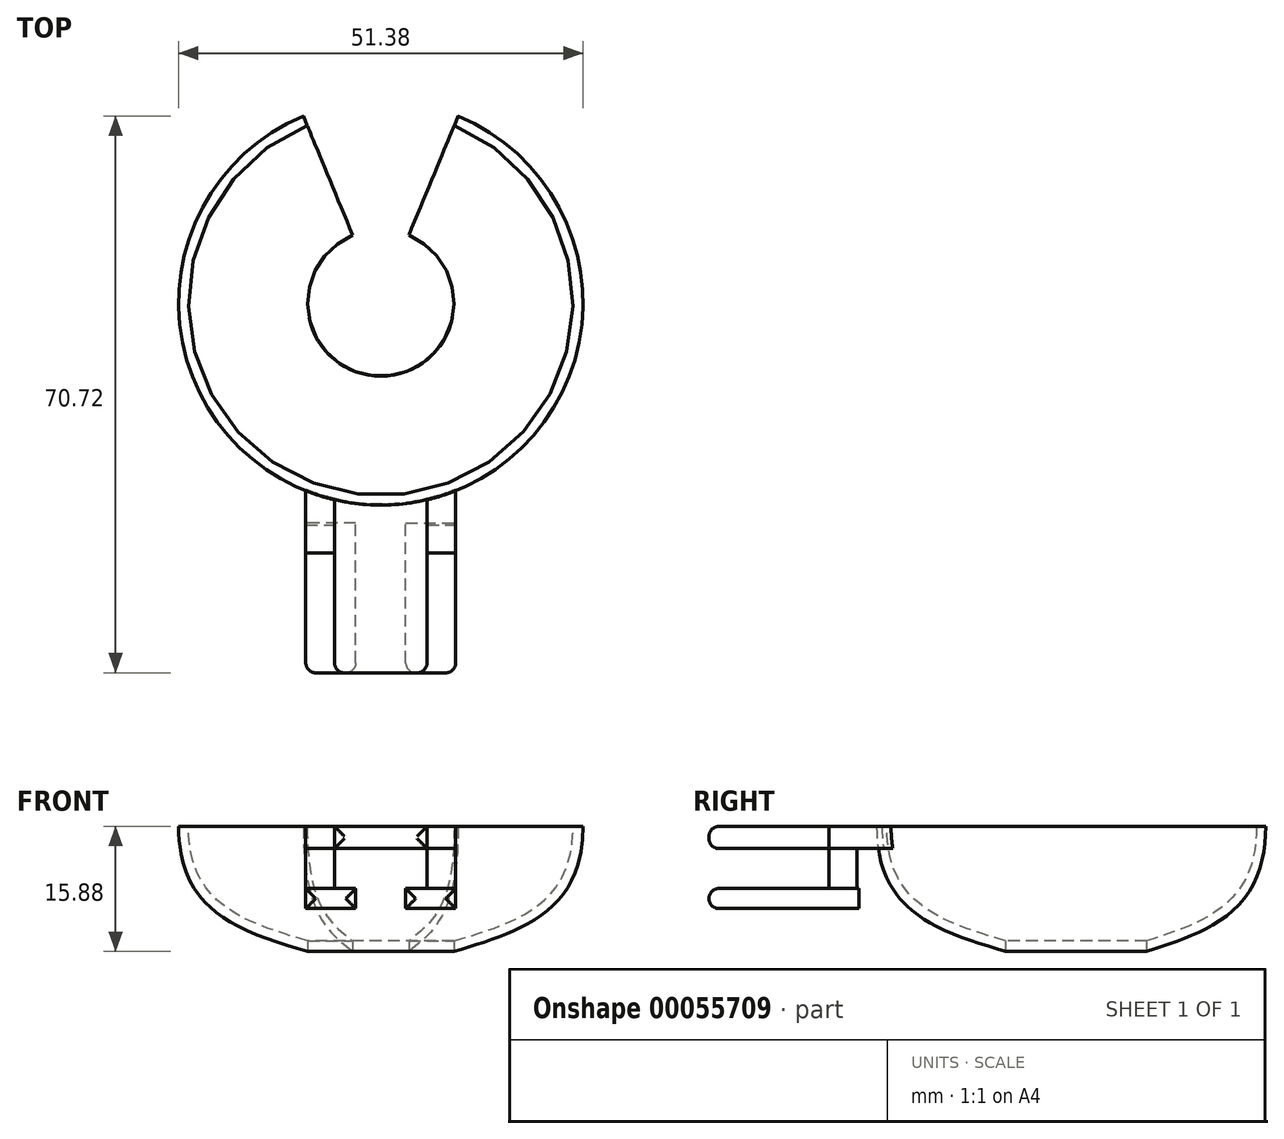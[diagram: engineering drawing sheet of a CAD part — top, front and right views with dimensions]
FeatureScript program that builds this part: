
annotation { "Feature Type Name" : "Feature", "Feature Type Description" : "" }
export const myFeature = defineFeature(function(context is Context, id is Id, definition is map)
    precondition{}
    {
        {
            var Q0;
            Q0=qCreatedBy(makeId("Top.planeOp"),FACE);
            var sketch = newSketch(context, id + "F0", { "sketchPlane" : qUnion([Q0])});
            skCircle(sketch, "E0", {"center": v(0, 0) * mm, "radius": 18.62 * mm});
            skSolve(sketch);
        }
        {
            var Q0;
            Q0=qCreatedBy(makeId("Top.planeOp"),FACE);
            cPlane(context, id + "F1", {"entities" : qUnion([Q0]), "cplaneType" : CPlaneType.OFFSET, "offset" : 31.75 * mm, "width" : 152.4 * mm, "height" : 152.4 * mm});
        }
        {
            var Q0;
            Q0=qCreatedBy(id+"F1.planeOp",FACE);
            var sketch = newSketch(context, id + "F2", { "sketchPlane" : qUnion([Q0])});
            skCircle(sketch, "E1", {"center": v(0, 0) * mm, "radius": 51.37 * mm});
            skSolve(sketch);
        }
        {
            var Q0;
            Q0=makeQuery(id+"F0.imprint","IMPRINT",FACE,{"disambiguationData":[TD([[makeQuery(id+"F0.imprint","IMPRINT",EDGE,{"derivedFrom":sQuery(id+"F0.wireOp",EDGE,"E0")}),1.0]])]});
            var Q1;
            Q1=makeQuery(id+"F2.imprint","IMPRINT",FACE,{"disambiguationData":[TD([[makeQuery(id+"F2.imprint","IMPRINT",EDGE,{"derivedFrom":sQuery(id+"F2.wireOp",EDGE,"E1")}),1.0]])]});
            loft(context, id + "F3", {"endCondition" : LoftEndDerivativeType.NORMAL_TO_PROFILE, "endMagnitude" : 2, "sheetProfilesArray" : [{ "sheetProfileEntities" : qUnion([Q0]) }, { "sheetProfileEntities" : qUnion([Q1]) }]});
        }
        {
            var Q0;
            Q0=makeQuery(id+"F3.opLoft","CAP_FACE",FACE,{"disambiguationData":[OSD([makeQuery(id+"F2.imprint","IMPRINT",FACE,{"disambiguationData":[TD([[makeQuery(id+"F2.imprint","IMPRINT",EDGE,{"derivedFrom":sQuery(id+"F2.wireOp",EDGE,"E1")}),1.0]])]})])],"isStart":true});
            shell(context, id + "F4", {"entities" : qUnion([Q0]), "thickness" : 2.54 * mm});
        }
        {
            var Q0;
            Q0=makeQuery(id+"F3.opLoft","CAP_FACE",FACE,{"disambiguationData":[OSD([makeQuery(id+"F0.imprint","IMPRINT",FACE,{"disambiguationData":[TD([[makeQuery(id+"F0.imprint","IMPRINT",EDGE,{"derivedFrom":sQuery(id+"F0.wireOp",EDGE,"E0")}),1.0]])]})])],"isStart":true});
            extrude(context, id + "F5", {"entities" : qUnion([Q0]), "operationType" : NewBodyOperationType.REMOVE, "oppositeDirection" : true, "depth" : 25.4 * mm});
        }
        {
            var Q0;
            Q0=qCreatedBy(makeId("Front.planeOp"),FACE);
            cPlane(context, id + "F6", {"entities" : qUnion([Q0]), "cplaneType" : CPlaneType.OFFSET, "offset" : 55.88 * mm, "width" : 152.4 * mm, "height" : 152.4 * mm});
        }
        {
            var Q0;
            Q0=qCreatedBy(id+"F6.planeOp",FACE);
            var sketch = newSketch(context, id + "F7", { "sketchPlane" : qUnion([Q0])});
            skLineSegment(sketch, "E2.rect.bottom", {"start": v(11.76, 26.12) * mm, "end": v(-11.76, 26.12) * mm});
            skLineSegment(sketch, "E2.rect.top", {"start": v(11.76, 31.75) * mm, "end": v(-11.76, 31.75) * mm});
            skLineSegment(sketch, "E2.rect.left", {"start": v(11.76, 26.12) * mm, "end": v(11.76, 31.75) * mm});
            skLineSegment(sketch, "E2.rect.right", {"start": v(-11.76, 26.12) * mm, "end": v(-11.76, 31.75) * mm});
            skPoint(sketch, "E2.rect.middle", {"position": v(0, 28.94) * mm});
            skLineSegment(sketch, "E3.bottom", {"start": v(6.35, 15.96) * mm, "end": v(19.05, 15.96) * mm});
            skLineSegment(sketch, "E3.top", {"start": v(6.35, 10.88) * mm, "end": v(19.05, 10.88) * mm});
            skLineSegment(sketch, "E3.left", {"start": v(6.35, 15.96) * mm, "end": v(6.35, 10.88) * mm});
            skLineSegment(sketch, "E3.right", {"start": v(19.05, 15.96) * mm, "end": v(19.05, 10.88) * mm});
            skLineSegment(sketch, "E4.bottom", {"start": v(-6.35, 15.96) * mm, "end": v(-19.05, 15.96) * mm});
            skLineSegment(sketch, "E4.top", {"start": v(-6.35, 10.88) * mm, "end": v(-19.05, 10.88) * mm});
            skLineSegment(sketch, "E4.left", {"start": v(-6.35, 15.96) * mm, "end": v(-6.35, 10.88) * mm});
            skLineSegment(sketch, "E4.right", {"start": v(-19.05, 15.96) * mm, "end": v(-19.05, 10.88) * mm});
            skLineSegment(sketch, "E5.bottom", {"start": v(11.76, 31.75) * mm, "end": v(19.05, 31.75) * mm});
            skLineSegment(sketch, "E5.top", {"start": v(11.76, 26.12) * mm, "end": v(19.05, 26.12) * mm});
            skLineSegment(sketch, "E5.left", {"start": v(11.76, 31.75) * mm, "end": v(11.76, 26.12) * mm});
            skLineSegment(sketch, "E5.right", {"start": v(19.05, 31.75) * mm, "end": v(19.05, 26.12) * mm});
            skLineSegment(sketch, "E6.bottom", {"start": v(-11.76, 31.75) * mm, "end": v(-19.05, 31.75) * mm});
            skLineSegment(sketch, "E6.top", {"start": v(-11.76, 26.12) * mm, "end": v(-19.05, 26.12) * mm});
            skLineSegment(sketch, "E6.left", {"start": v(-11.76, 31.75) * mm, "end": v(-11.76, 26.12) * mm});
            skLineSegment(sketch, "E6.right", {"start": v(-19.05, 31.75) * mm, "end": v(-19.05, 26.12) * mm});
            skSolve(sketch);
        }
        {
            var Q0;
            Q0=makeQuery(id+"F7.imprint","IMPRINT",FACE,{"disambiguationData":[TD([[makeQuery(id+"F7.imprint","IMPRINT",EDGE,{"derivedFrom":sQuery(id+"F7.wireOp",EDGE,"E4.bottom")}),1.0]])]});
            var Q1;
            Q1=makeQuery(id+"F7.imprint","IMPRINT",FACE,{"disambiguationData":[TD([[makeQuery(id+"F7.imprint","IMPRINT",EDGE,{"derivedFrom":sQuery(id+"F7.wireOp",EDGE,"E3.bottom")}),-1.0]])]});
            extrude(context, id + "F8", {"entities" : qUnion([Q0, Q1]), "depth" : 38.1 * mm});
        }
        {
            var Q0;
            Q0=qCreatedBy(makeId("Right.planeOp"),FACE);
            var sketch = newSketch(context, id + "F9", { "sketchPlane" : qUnion([Q0])});
            skLineSegment(sketch, "E7.bottom", {"start": v(0, 57.73) * mm, "end": v(69.76, 57.73) * mm});
            skLineSegment(sketch, "E7.top", {"start": v(0, -10.02) * mm, "end": v(69.76, -10.02) * mm});
            skLineSegment(sketch, "E7.left", {"start": v(0, 57.73) * mm, "end": v(0, -10.02) * mm});
            skLineSegment(sketch, "E7.right", {"start": v(69.76, 57.73) * mm, "end": v(69.76, -10.02) * mm});
            skSolve(sketch);
        }
        {
            var Q0;
            Q0 = qSketchRegion(id + "F9", true);
            var Q1;
            Q1=sQuery(id+"F9.wireOp",EDGE,"E7.left");
            revolve(context, id + "F10", {"operationType" : NewBodyOperationType.REMOVE, "entities" : qUnion([Q0]), "axis" : qUnion([Q1]), "revolveType" : RevolveType.SYMMETRIC, "oppositeDirection" : true, "angle" : 45 * degree});
        }
        {
            var Q0;
            Q0=makeQuery(id+"F7.imprint","IMPRINT",FACE,{"disambiguationData":[TD([[makeQuery(id+"F7.imprint","IMPRINT",EDGE,{"derivedFrom":sQuery(id+"F7.wireOp",EDGE,"E5.bottom")}),-1.0]])]});
            var Q1;
            Q1=makeQuery(id+"F7.imprint","IMPRINT",FACE,{"disambiguationData":[TD([[makeQuery(id+"F7.imprint","IMPRINT",EDGE,{"derivedFrom":sQuery(id+"F7.wireOp",EDGE,"E6.bottom")}),1.0]])]});
            var Q2;
            Q2=makeQuery(id+"F3.opLoft","SWEPT_BODY",BODY,{"disambiguationData":[OSD([makeQuery(id+"F0.imprint","IMPRINT",FACE,{"disambiguationData":[TD([[makeQuery(id+"F0.imprint","IMPRINT",EDGE,{"derivedFrom":sQuery(id+"F0.wireOp",EDGE,"E0")}),1.0]])]}),makeQuery(id+"F2.imprint","IMPRINT",FACE,{"disambiguationData":[TD([[makeQuery(id+"F2.imprint","IMPRINT",EDGE,{"derivedFrom":sQuery(id+"F2.wireOp",EDGE,"E1")}),1.0]])]})])]});
            extrude(context, id + "F11", {"entities" : qUnion([Q0, Q1]), "endBound" : BoundingType.UP_TO_NEXT, "oppositeDirection" : true, "endBoundEntityBody" : qUnion([Q2]), "depth" : 25.4 * mm, "hasSecondDirection" : true, "secondDirectionOppositeDirection" : false, "secondDirectionDepth" : 7.62 * mm});
        }
        {
            var Q0;
            Q0=makeQuery(id+"F7.imprint","IMPRINT",FACE,{"disambiguationData":[TD([[makeQuery(id+"F7.imprint","IMPRINT",EDGE,{"derivedFrom":sQuery(id+"F7.wireOp",EDGE,"E2.rect.bottom")}),-1.0]])]});
            extrude(context, id + "F12", {"entities" : qUnion([Q0]), "endBound" : BoundingType.UP_TO_NEXT, "oppositeDirection" : true, "depth" : 25.4 * mm, "hasSecondDirection" : true, "secondDirectionOppositeDirection" : false, "secondDirectionDepth" : 38.1 * mm});
        }
        {
            var Q0;
            Q0=makeQuery(id+"F11.opExtrude","SWEPT_FACE",FACE,{"disambiguationData":[OSD([sQuery(id+"F7.wireOp",EDGE,"E5.top")])]});
            var sketch = newSketch(context, id + "F13", { "sketchPlane" : qUnion([Q0])});
            skPoint(sketch, "E8.0", {"position": v(-19.05, 63.5) * mm});
            skPoint(sketch, "E9.0", {"position": v(-11.76, 63.5) * mm});
            skPoint(sketch, "E10.0", {"position": v(11.76, 63.5) * mm});
            skPoint(sketch, "E11.0", {"position": v(19.05, 63.5) * mm});
            skLineSegment(sketch, "E12.bottom", {"start": v(19.05, 63.5) * mm, "end": v(11.76, 63.5) * mm});
            skLineSegment(sketch, "E12.top", {"start": v(19.05, 56.4) * mm, "end": v(11.76, 56.4) * mm});
            skLineSegment(sketch, "E12.left", {"start": v(19.05, 63.5) * mm, "end": v(19.05, 56.4) * mm});
            skLineSegment(sketch, "E12.right", {"start": v(11.76, 63.5) * mm, "end": v(11.76, 56.4) * mm});
            skLineSegment(sketch, "E13.bottom", {"start": v(-19.05, 63.5) * mm, "end": v(-11.76, 63.5) * mm});
            skLineSegment(sketch, "E13.top", {"start": v(-19.05, 56.4) * mm, "end": v(-11.76, 56.4) * mm});
            skLineSegment(sketch, "E13.left", {"start": v(-19.05, 63.5) * mm, "end": v(-19.05, 56.4) * mm});
            skLineSegment(sketch, "E13.right", {"start": v(-11.76, 63.5) * mm, "end": v(-11.76, 56.4) * mm});
            skSolve(sketch);
        }
        {
            var Q0;
            Q0 = qSketchRegion(id + "F13", true);
            extrude(context, id + "F14", {"entities" : qUnion([Q0]), "endBound" : BoundingType.UP_TO_NEXT, "depth" : 25.4 * mm});
        }
        {
            var Q0;
            Q0=makeQuery(id+"F12.opExtrude","CAP_FACE",FACE,{"disambiguationData":[OSD([sQuery(id+"F7.wireOp",EDGE,"E2.rect.bottom"),sQuery(id+"F7.wireOp",EDGE,"E2.rect.top"),sQuery(id+"F7.wireOp",EDGE,"E5.left"),sQuery(id+"F7.wireOp",EDGE,"E6.left")])],"isStart":true});
            var Q1;
            Q1=makeQuery(id+"F8.opExtrude","CAP_FACE",FACE,{"disambiguationData":[OSD([sQuery(id+"F7.wireOp",EDGE,"E4.bottom"),sQuery(id+"F7.wireOp",EDGE,"E4.top"),sQuery(id+"F7.wireOp",EDGE,"E4.left"),sQuery(id+"F7.wireOp",EDGE,"E4.right")])],"isStart":false});
            var Q2;
            Q2=makeQuery(id+"F8.opExtrude","CAP_FACE",FACE,{"disambiguationData":[OSD([sQuery(id+"F7.wireOp",EDGE,"E3.bottom"),sQuery(id+"F7.wireOp",EDGE,"E3.top"),sQuery(id+"F7.wireOp",EDGE,"E3.left"),sQuery(id+"F7.wireOp",EDGE,"E3.right")])],"isStart":false});
            fillet(context, id + "F15", {"entities" : qUnion([Q0, Q1, Q2]), "radius" : 2.54 * mm, "tangentPropagation" : true, "allowEdgeOverflow" : false});
        }
        {
            var Q0;
            Q0=makeQuery(id+"F3.opLoft","SWEPT_BODY",BODY,{"disambiguationData":[OSD([makeQuery(id+"F0.imprint","IMPRINT",FACE,{"disambiguationData":[TD([[makeQuery(id+"F0.imprint","IMPRINT",EDGE,{"derivedFrom":sQuery(id+"F0.wireOp",EDGE,"E0")}),1.0]])]}),makeQuery(id+"F2.imprint","IMPRINT",FACE,{"disambiguationData":[TD([[makeQuery(id+"F2.imprint","IMPRINT",EDGE,{"derivedFrom":sQuery(id+"F2.wireOp",EDGE,"E1")}),1.0]])]})])]});
            var Q1;
            Q1=makeQuery(id+"F8.opExtrude","SWEPT_BODY",BODY,{"disambiguationData":[OSD([sQuery(id+"F7.wireOp",EDGE,"E3.bottom"),sQuery(id+"F7.wireOp",EDGE,"E3.top"),sQuery(id+"F7.wireOp",EDGE,"E3.left"),sQuery(id+"F7.wireOp",EDGE,"E3.right")])]});
            var Q2;
            Q2=makeQuery(id+"F8.opExtrude","SWEPT_BODY",BODY,{"disambiguationData":[OSD([sQuery(id+"F7.wireOp",EDGE,"E4.bottom"),sQuery(id+"F7.wireOp",EDGE,"E4.top"),sQuery(id+"F7.wireOp",EDGE,"E4.left"),sQuery(id+"F7.wireOp",EDGE,"E4.right")])]});
            var Q3;
            Q3=makeQuery(id+"F11.opExtrude","SWEPT_BODY",BODY,{"disambiguationData":[OSD([sQuery(id+"F7.wireOp",EDGE,"E5.bottom"),sQuery(id+"F7.wireOp",EDGE,"E5.top"),sQuery(id+"F7.wireOp",EDGE,"E5.left"),sQuery(id+"F7.wireOp",EDGE,"E5.right")])]});
            var Q4;
            Q4=makeQuery(id+"F14.opExtrude","SWEPT_BODY",BODY,{"disambiguationData":[OSD([sQuery(id+"F13.wireOp",EDGE,"E13.bottom"),sQuery(id+"F13.wireOp",EDGE,"E13.top"),sQuery(id+"F13.wireOp",EDGE,"E13.left"),sQuery(id+"F13.wireOp",EDGE,"E13.right")])]});
            var Q5;
            Q5=makeQuery(id+"F14.opExtrude","SWEPT_BODY",BODY,{"disambiguationData":[OSD([sQuery(id+"F13.wireOp",EDGE,"E12.bottom"),sQuery(id+"F13.wireOp",EDGE,"E12.top"),sQuery(id+"F13.wireOp",EDGE,"E12.left"),sQuery(id+"F13.wireOp",EDGE,"E12.right")])]});
            var Q6;
            Q6=makeQuery(id+"F12.opExtrude","SWEPT_BODY",BODY,{"disambiguationData":[OSD([sQuery(id+"F7.wireOp",EDGE,"E2.rect.bottom"),sQuery(id+"F7.wireOp",EDGE,"E2.rect.top"),sQuery(id+"F7.wireOp",EDGE,"E5.left"),sQuery(id+"F7.wireOp",EDGE,"E6.left")])]});
            var Q7;
            Q7=makeQuery(id+"F11.opExtrude","SWEPT_BODY",BODY,{"disambiguationData":[OSD([sQuery(id+"F7.wireOp",EDGE,"E6.bottom"),sQuery(id+"F7.wireOp",EDGE,"E6.top"),sQuery(id+"F7.wireOp",EDGE,"E6.left"),sQuery(id+"F7.wireOp",EDGE,"E6.right")])]});
            var Q8;
            Q8=qCreatedBy(makeId("Origin.pointOp"),VERTEX);
            transform(context, id + "F16", {"entities" : qUnion([Q0, Q1, Q2, Q3, Q4, Q5, Q6, Q7]), "transformType" : TransformType.SCALE_UNIFORMLY, "scale" : 0.5, "scalePoint" : qUnion([Q8]), "makeCopy" : false});
        }
    });
